# Revit family: QF_ELECTROLUXPROFESSIONAL_1LSN97_WH6-33_S
name_source: partatom
category: Attrezzature speciali
units: mm (PartAtom-declared; Revit-internal decimal feet)

## family parameters
Basato su piano di lavoro = No
Condiviso = No
Punto di calcolo locali = No
Quota connettore circolare = Usa diametro
Sempre verticale = Sì
Taglio con vuoti quando caricato = No
Tipo di parte = Normale

## types (5) — shared parameters
Depth Actual = 1134 mm  [stored 3.72047 ft]
Height Actual = 1446 mm  [stored 4.74409 ft]
Latent Heat Output = 0.0
Length Actual = 1020 mm  [stored 3.34646 ft]
Modello = WH6-33
Produttore = Electrolux Professional
Sensible Heat Output = 0.0
URL = www.electroluxprofessional.com
Weight = 560
zero-valued in all types: Gas KW, Prospetto di default, Steam Pounds per Hour

## per-type parameters (varying)
| type | Cycle | Descrizione | Item Number | Phase | Volts | Watts |
| 9868130133 | 50 Hz | WASHER WH6-33 33KG STEAM 200/50/60/3 COMPASS PRO 6H43 JP,EN 2xWATER POWDER+5xLIQ. VALV.OPEN SST/SILVER 2.I/O DISCON. | 1L0HG8 | 3 | 200 V | 3100 W |
| 9868130330 | 60 Hz | WASHER WH6-33 33KG STEAM 220-240/60/1N COMPASS PRO 6G01 ML 2xWATER POWDER+5xLIQ. VALV.OPEN SILVER 2.I/O DISCON. STOP | 1L0H7F | 1 | 240 V | 3500 W |
| 9868130190 | 50 Hz | WASHER WH6-33 33KG STEAM 220-240/50/1N COMPASS PRO 6G01 ML 2xWATER POWDER+5xLIQ. VALV.OPEN SILVER 2.I/O DISCON. STOP | 1LA1B9 | 1 | 240 V | 3500 W |
| 9868130176 | 50 Hz | WASHER WH6-33 33KG STEAM 220-240/50/1N COMPASS PRO 6G01 CH-EN 2xWATER POWDER+5xLIQ. VALV.OPEN SILVER 2.I/O DISCON. STOP | 1L0GCF | 1 | 240 V | 3500 W |
| 9868130161 | 50 Hz | WASHER WH6-33 33KG STEAM 200/50/60/3 COMPASS PRO 6H43 JP,EN 2xWATER POWDER+5xLIQ. VALV.OPEN SILVER 2.I/O DISCON. | 1L822M | 3 | 200 V | 3100 W |

note: [stored X ft] marks values corroborated as IEEE doubles in the binary element streams (Revit-internal decimal feet)

## geometry (parser evidence)
native form markers: Blend x8
no freeform markers — native parametric forms only
